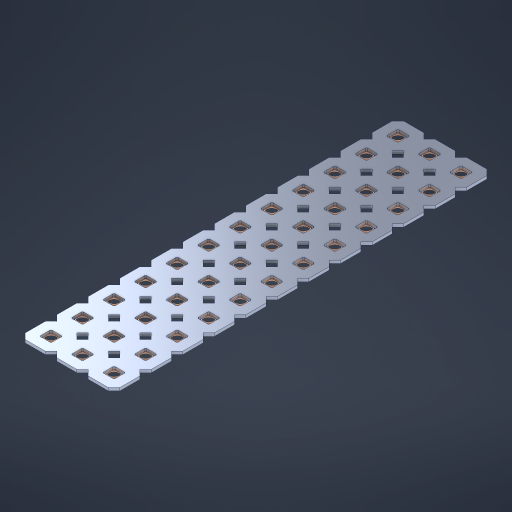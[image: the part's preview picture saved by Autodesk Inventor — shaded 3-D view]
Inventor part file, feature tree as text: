
AUTODESK INVENTOR PART (.ipt)
format: ipt  version: 2023 (Build 270158000, 158)  size: 673,792 bytes
history: native  units: in
note: dims shown in document units (in); Inventor stores cm internally (conversion verified against a paired STEP export)
features: other x37, extrude x35, sketch x2, pattern_linear x1
ambient origin geometry x8: Origin, YZ Plane, XZ Plane, XY Plane, X Axis, Y Axis, Z Axis, Center Point
bodies: Solid1 (feature_tree), Body (feature_tree)
feature tree (75):
  pattern_linear  "Rectangular Pattern1"  Spacing1=0.09in  [1 undecoded]
  sketch  "Sketch1"  dims[d1=0.5in]
  sketch  "Sketch2"  dims[d2=0.182in d3=0.09in d4=0.09in d5=0.09in d6=0.09in d7=0.09in d8=0.09in d9=0.09in d10=0.09in d11=0.02in d13=0.0in d14=0.172in d15=0.0625in d16=0.0in d19=0.5in d22=0.5in]
  other  "Srf1"
  other  "Srf126"
  other  "Srf127"
  other  "Srf128"
  other  "Srf129"
  other  "Srf130"
  other  "Srf131"
  other  "Srf250"
  other  "Srf251"
  other  "Srf252"
  other  "Srf253"
  other  "Srf254"
  other  "Srf268"
  other  "Srf269"
  other  "Srf270"
  other  "Srf271"
  other  "Srf272"
  other  "Srf273"
  other  "Srf274"
  other  "Srf275"
  other  "Srf276"
  other  "Srf277"
  other  "Srf278"
  other  "Srf279"
  other  "Srf293"
  other  "Srf294"
  other  "Srf295"
  other  "Srf296"
  other  "Srf297"
  other  "Srf298"
  other  "Srf299"
  other  "Srf300"
  other  "Srf301"
  other  "Srf302"
  other  "Srf303"
  other  "Srf304"
  other  "Circle"
  extrude  "ExtrusionSrf126"  Depth=0.09in
  extrude  "ExtrusionSrf127"  Depth=0.09in
  extrude  "ExtrusionSrf128"  Depth=0.09in
  extrude  "ExtrusionSrf129"  Depth=0.09in
  extrude  "ExtrusionSrf130"  Depth=0.09in
  extrude  "ExtrusionSrf131"  Depth=0.09in
  extrude  "ExtrusionSrf250"  Depth=0.09in
  extrude  "ExtrusionSrf251"  Depth=0.02in
  extrude  "ExtrusionSrf252"  TaperAngle=0.0deg  [1 undecoded]
  extrude  "ExtrusionSrf253"  Depth=0.5in
  extrude  "ExtrusionSrf254"  Depth=0.5in TaperAngle=0.0deg
  extrude  "ExtrusionSrf268"  Depth=0.5in
  extrude  "ExtrusionSrf269"  Depth=0.5in
  extrude  "ExtrusionSrf270"  [1 undecoded]
  extrude  "ExtrusionSrf271"  [1 undecoded]
  extrude  "ExtrusionSrf272"  [1 undecoded]
  extrude  "ExtrusionSrf273"  [1 undecoded]
  extrude  "ExtrusionSrf274"  [1 undecoded]
  extrude  "ExtrusionSrf275"  [1 undecoded]
  extrude  "ExtrusionSrf276"  [1 undecoded]
  extrude  "ExtrusionSrf277"  [1 undecoded]
  extrude  "ExtrusionSrf278"  [1 undecoded]
  extrude  "ExtrusionSrf279"  [1 undecoded]
  extrude  "ExtrusionSrf293"  [1 undecoded]
  extrude  "ExtrusionSrf294"  [1 undecoded]
  extrude  "ExtrusionSrf295"  [1 undecoded]
  extrude  "ExtrusionSrf296"  [1 undecoded]
  extrude  "ExtrusionSrf297"  [1 undecoded]
  extrude  "ExtrusionSrf298"  [1 undecoded]
  extrude  "ExtrusionSrf299"  [1 undecoded]
  extrude  "ExtrusionSrf300"  [1 undecoded]
  extrude  "ExtrusionSrf301"  [1 undecoded]
  extrude  "ExtrusionSrf302"  [1 undecoded]
  extrude  "ExtrusionSrf303"  [1 undecoded]
  extrude  "ExtrusionSrf304"  [1 undecoded]
note: 24 required parameter values undecoded (feature->parameter linkage not recoverable at this tier; creation-order binding heuristic only, values carry confidence <= 0.55)
